# Revit family: Hager-Orion_Inox-IP66-D150-Cl.I-Inox_encl-630A-300mm-NoHosted-PL-en
name_source: partatom
category: Electrical Equipment
units: mm (PartAtom-declared; Revit-internal decimal feet)

## family parameters
Always vertical = Yes
Cut with Voids When Loaded = No
Panel Configuration = Two Columns, Circuits Across
Part Type = Panelboard
Room Calculation Point = No
Round Connector Dimension = Use Diameter
Shared = No
Work Plane-Based = Yes

## types (4) — shared parameters
Default Elevation = 1219 mm
EF000003 - Mounting method = EV000384 - Surface mounted (plaster)
EF000007 - Colour = EV000154 - Other
EF000040 - Height = 300 mm
EF000049 - Depth = 150 mm  [stored 0.492126 ft]
EF000118 - With mounting plate = No
EF000339 - Type of cover = EV004216 - Door
EF001088 - Extension possible = Yes
EF001131 - Internal depth = 116 mm  [stored 0.380577 ft]
EF001596 - Material housing = EV000166 - Stainless steel
EF003532 - Suitable for outdoor use = Yes
EF004293 - Impact strength = EV008784 - IK10
EF004464 - Type of door = EV002646 - Single
EF005474 - Degree of protection (IP) = EV006422 - IP66
EF006244 - Transparent cover/door = No
EF007800 - Suitable for lightning protection = No
EF008873 - Nominal current (In) = 630 A
EF009170 - Material plate thickness cabinet = 2 mm  [stored 0.00656168 ft]
EF009171 - Material plate thickness door/cover = 2 mm  [stored 0.00656168 ft]
EF015940 - Cover with overpressure release = No
HG000002 - With door or cover = Yes
HG000003 - Range = Orion Inox
HG000006 - Flush mounted = No
HG000009 - Double swing door = No
HG000010 - Asymmetric doors = No
HG000023 - Double section enclosure = No
HG000024 - Bottom section height = 600 mm
HG000026 - Floor standing = No
Manufacturer = Hager
Type Comments = Orion Inox
zero-valued in all types: EF000218 - Built-in depth, EF000266 - Number of rows, EF000437 - Number of conduit inlets, EF002950 - Width in number of modular spacings, EF004427 - Number of modules, EF009554 - Number of openings for flange plates, HG000027 - Plinth height

## per-type parameters (varying)
| type | EF000008 - Width | EF001613 - Circuit integrity | EF006306 - With lock | EF009212 - Cover model | HG000004 - Manufacturer reference |
| Surface mounted (plaster) IP66 W200 H300 D150  - FL010BW | 200 mm  [stored 0.656168 ft] |  | No | EV009916 - With notch | FL010BW |
| Surface mounted (plaster) IP66 W200 H300 D150  - FL010BWL | 200 mm  [stored 0.656168 ft] |  | No | EV009916 - With notch | FL010BWL |
| Surface mounted (plaster) IP66 W400 H300 D150  - FL013BW | 400 mm  [stored 1.31234 ft] | EV000494 - None | Yes | EV000116 - Closed | FL013BW |
| Surface mounted (plaster) IP66 W400 H300 D150  - FL013BWL | 400 mm  [stored 1.31234 ft] | EV000494 - None | Yes | EV000116 - Closed | FL013BWL |

note: [stored X ft] marks values corroborated as IEEE doubles in the binary element streams (Revit-internal decimal feet)

## geometry (parser evidence)
native form markers: Blend x4, Sweep x8
no freeform markers — native parametric forms only
